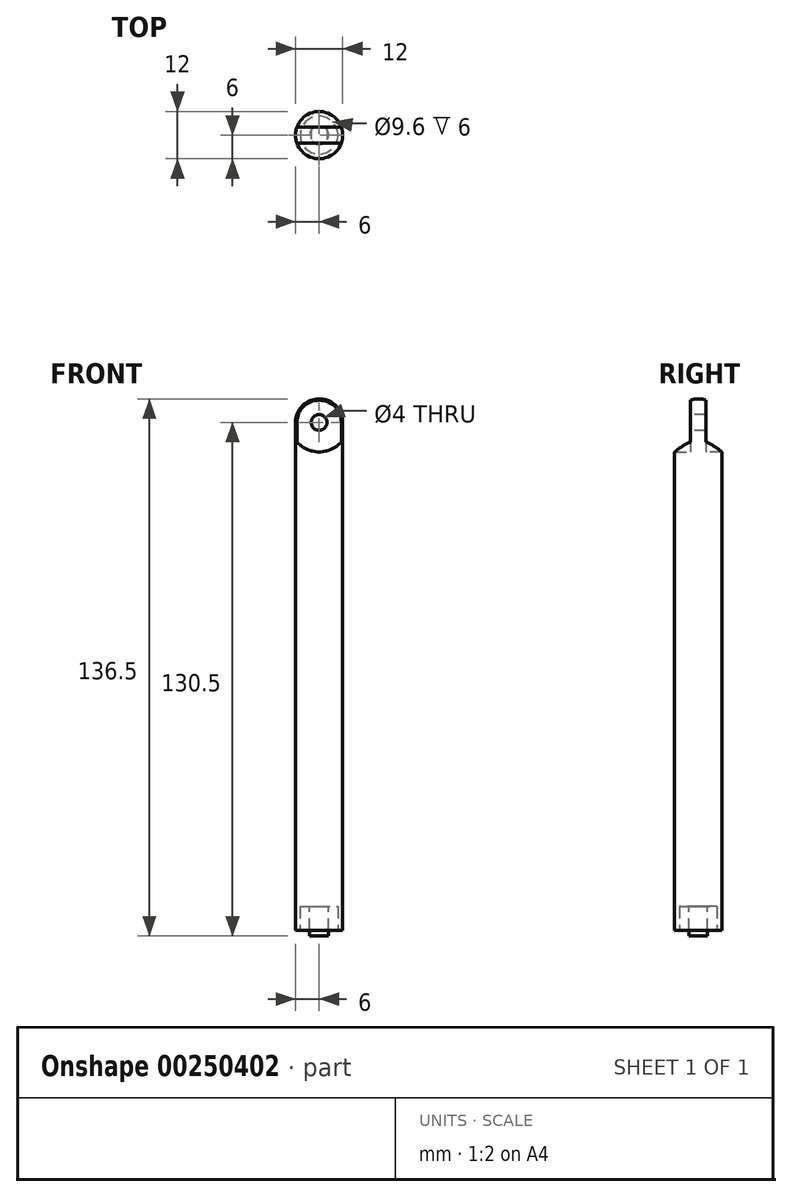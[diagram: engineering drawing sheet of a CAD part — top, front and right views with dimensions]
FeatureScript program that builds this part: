
annotation { "Feature Type Name" : "Feature", "Feature Type Description" : "" }
export const myFeature = defineFeature(function(context is Context, id is Id, definition is map)
    precondition{}
    {
        {
            var Q0;
            Q0=qCreatedBy(makeId("Top.planeOp"),FACE);
            var sketch = newSketch(context, id + "F0", { "sketchPlane" : qUnion([Q0])});
            skCircle(sketch, "E0", {"center": v(0, 0) * mm, "radius": 6 * mm});
            skSolve(sketch);
        }
        {
            var Q0;
            Q0 = qSketchRegion(id + "F0", true);
            extrude(context, id + "F1", {"entities" : qUnion([Q0]), "depth" : 135 * mm});
        }
        {
            var Q0;
            Q0=qCreatedBy(makeId("Front.planeOp"),FACE);
            var sketch = newSketch(context, id + "F2", { "sketchPlane" : qUnion([Q0])});
            skArc(sketch, "E1", {"start": v(-6.02, 124.53) * mm, "mid": v(0.12, 121.5) * mm, "end": v(6.16, 124.73) * mm});
            skLineSegment(sketch, "E2", {"start": v(-6.02, 135.02) * mm, "end": v(6.16, 135.02) * mm});
            skLineSegment(sketch, "E3", {"start": v(6.16, 135.02) * mm, "end": v(6.16, 124.73) * mm});
            skLineSegment(sketch, "E4", {"start": v(-6.02, 135.02) * mm, "end": v(-6.02, 124.53) * mm});
            skSolve(sketch);
        }
        {
            var Q0;
            Q0 = qSketchRegion(id + "F2", true);
            extrude(context, id + "F3", {"entities" : qUnion([Q0]), "operationType" : NewBodyOperationType.REMOVE, "endBound" : BoundingType.UP_TO_NEXT, "oppositeDirection" : true, "depth" : 6 * mm, "hasSecondDirection" : true, "secondDirectionOppositeDirection" : true, "secondDirectionDepth" : 2 * mm});
        }
        {
            var Q0;
            Q0 = qSketchRegion(id + "F2", true);
            extrude(context, id + "F4", {"entities" : qUnion([Q0]), "operationType" : NewBodyOperationType.REMOVE, "depth" : 6 * mm, "hasSecondDirection" : true, "secondDirectionOppositeDirection" : false, "secondDirectionDepth" : 2 * mm});
        }
        {
            var Q0;
            Q0=makeQuery(id+"F4.boolean.opBoolean","SPLIT",EDGE,{"disambiguationData":[OD(1.0)],"derivedFrom":makeQuery(id+"F1.opExtrude","CAP_EDGE",EDGE,{"disambiguationData":[OSD([sQuery(id+"F0.wireOp",EDGE,"E0")])],"isStart":false})});
            fillet(context, id + "F5", {"entities" : qUnion([Q0]), "radius" : 6 * mm, "tangentPropagation" : true, "allowEdgeOverflow" : false});
        }
        {
            var Q0;
            Q0=makeQuery(id+"F2.imprint","IMPRINT",FACE,{"disambiguationData":[TD([[makeQuery(id+"F2.imprint","IMPRINT",EDGE,{"derivedFrom":sQuery(id+"F2.wireOp",EDGE,"E1")}),1.0]])]});
            var sketch = newSketch(context, id + "F6", { "sketchPlane" : qUnion([Q0])});
            skCircle(sketch, "E5", {"center": v(0, 129) * mm, "radius": 2 * mm});
            skSolve(sketch);
        }
        {
            var Q0;
            Q0 = qSketchRegion(id + "F6", true);
            extrude(context, id + "F7", {"entities" : qUnion([Q0]), "operationType" : NewBodyOperationType.REMOVE, "endBound" : BoundingType.SYMMETRIC, "oppositeDirection" : true, "depth" : 25 * mm});
        }
        {
            var Q0;
            Q0=makeQuery(id+"F1.opExtrude","CAP_FACE",FACE,{"disambiguationData":[OSD([sQuery(id+"F0.wireOp",EDGE,"E0")])],"isStart":true});
            var sketch = newSketch(context, id + "F8", { "sketchPlane" : qUnion([Q0])});
            skCircle(sketch, "E6", {"center": v(0, 0) * mm, "radius": 4.8 * mm});
            skSolve(sketch);
        }
        {
            var Q0;
            Q0 = qSketchRegion(id + "F8", true);
            extrude(context, id + "F9", {"entities" : qUnion([Q0]), "operationType" : NewBodyOperationType.REMOVE, "oppositeDirection" : true, "depth" : 6 * mm});
        }
        {
            var Q0;
            Q0=makeQuery(id+"F9.boolean.opBoolean","COPY",FACE,{"derivedFrom":makeQuery(id+"F9.opExtrude","CAP_FACE",FACE,{"disambiguationData":[OSD([sQuery(id+"F8.wireOp",EDGE,"E6")])],"isStart":false})});
            var sketch = newSketch(context, id + "F10", { "sketchPlane" : qUnion([Q0])});
            skCircle(sketch, "E7", {"center": v(0, 0) * mm, "radius": 2.37 * mm});
            skSolve(sketch);
        }
        {
            var Q0;
            Q0 = qSketchRegion(id + "F10", true);
            extrude(context, id + "F11", {"entities" : qUnion([Q0]), "operationType" : NewBodyOperationType.ADD, "depth" : 7.5 * mm});
        }
    });
